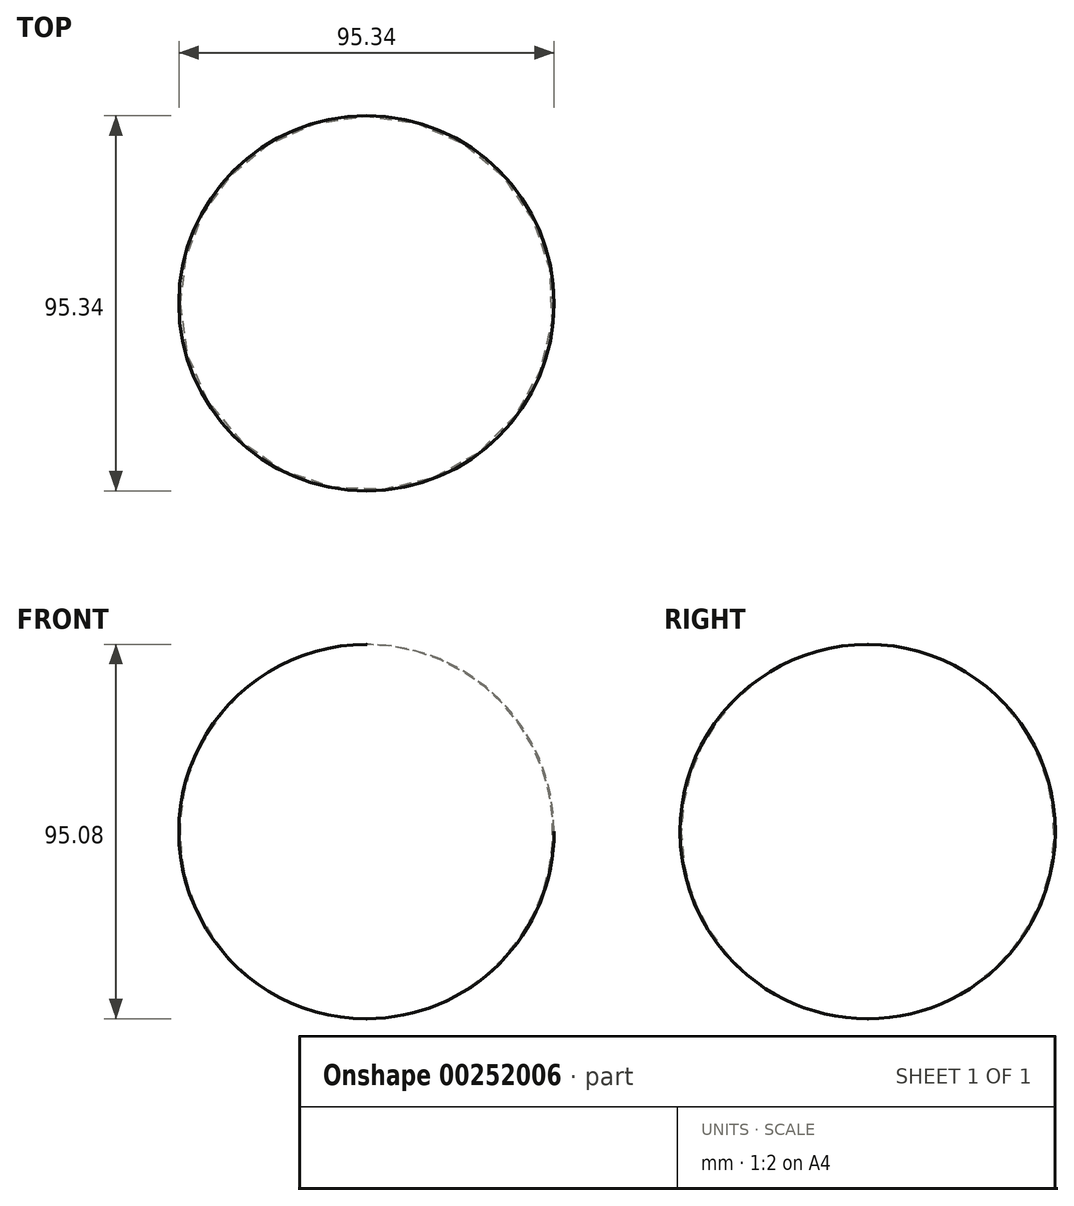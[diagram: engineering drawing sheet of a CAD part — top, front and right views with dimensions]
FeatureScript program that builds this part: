
annotation { "Feature Type Name" : "Feature", "Feature Type Description" : "" }
export const myFeature = defineFeature(function(context is Context, id is Id, definition is map)
    precondition{}
    {
        {
            var Q0;
            Q0=qCreatedBy(makeId("Front.planeOp"),FACE);
            var sketch = newSketch(context, id + "F0", { "sketchPlane" : qUnion([Q0])});
            skArc(sketch, "E0", {"start": v(0, 51.07) * mm, "mid": v(-47.67, 3.53) * mm, "end": v(0, -44) * mm});
            skPoint(sketch, "E1.start.orphan", {"position": v(0, 70.6) * mm});
            skLineSegment(sketch, "E2", {"start": v(0, 70.6) * mm, "end": v(0, -65.9) * mm});
            skSolve(sketch);
        }
        {
            var Q0;
            {var subQ0=sQuery(id+"F0.wireOp",EDGE,"E0");Q0=makeQuery(id+"F0.imprint","IMPRINT",FACE,{"disambiguationData":[TD([[makeQuery(id+"F0.imprint","IMPRINT",EDGE,{"derivedFrom":subQ0}),1.0]])]});}
            var Q1;
            Q1=sQuery(id+"F0.wireOp",EDGE,"E2");
            revolve(context, id + "F1", {"entities" : qUnion([Q0]), "axis" : qUnion([Q1]), "revolveType" : RevolveType.FULL});
        }
    });
